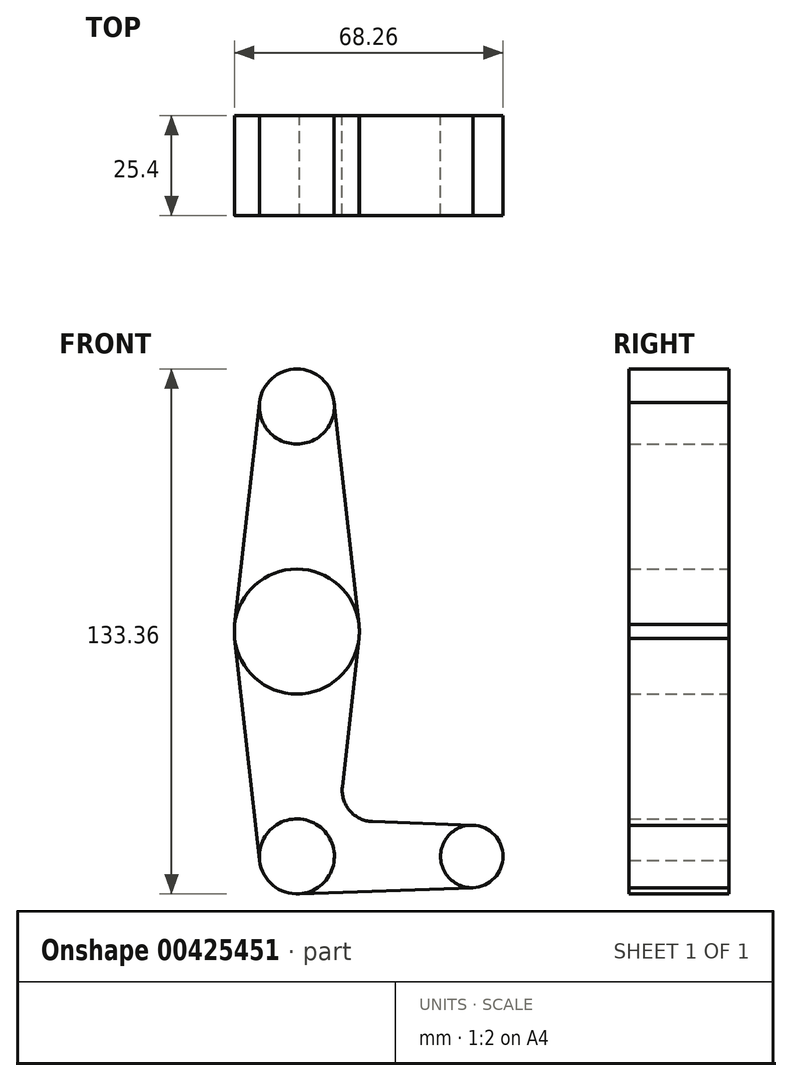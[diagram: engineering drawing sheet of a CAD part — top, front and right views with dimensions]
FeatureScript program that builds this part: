
annotation { "Feature Type Name" : "Feature", "Feature Type Description" : "" }
export const myFeature = defineFeature(function(context is Context, id is Id, definition is map)
    precondition{}
    {
        {
            var Q0;
            Q0=qCreatedBy(makeId("Front.planeOp"),FACE);
            var sketch = newSketch(context, id + "F0", { "sketchPlane" : qUnion([Q0])});
            skLineSegment(sketch, "E0", {"start": v(0, 114.3) * mm, "end": v(0, 0) * mm, "construction": true});
            skLineSegment(sketch, "E1", {"start": v(0, 0) * mm, "end": v(44.45, 0) * mm, "construction": true});
            skCircle(sketch, "E2", {"center": v(0, 114.3) * mm, "radius": 9.53 * mm});
            skCircle(sketch, "E3", {"center": v(0, 57.15) * mm, "radius": 15.88 * mm});
            skCircle(sketch, "E4", {"center": v(0, 0) * mm, "radius": 9.53 * mm});
            skCircle(sketch, "E5", {"center": v(44.45, 0) * mm, "radius": 7.94 * mm});
            skLineSegment(sketch, "E6", {"start": v(-9.47, 115.36) * mm, "end": v(-15.78, 58.91) * mm});
            skLineSegment(sketch, "E7", {"start": v(9.47, 115.36) * mm, "end": v(15.78, 58.91) * mm});
            skLineSegment(sketch, "E8", {"start": v(-15.78, 55.39) * mm, "end": v(-9.58, 0) * mm});
            skLineSegment(sketch, "E9", {"start": v(15.78, 55.39) * mm, "end": v(11.56, 17.67) * mm});
            skLineSegment(sketch, "E10", {"start": v(0, -9.52) * mm, "end": v(44.73, -7.93) * mm});
            skLineSegment(sketch, "E11", {"start": v(19.18, 8.85) * mm, "end": v(44.73, 7.93) * mm});
            skArc(sketch, "E12.filletArc", {"start": v(11.56, 17.67) * mm, "mid": v(13.44, 11.6) * mm, "end": v(19.18, 8.85) * mm});
            skLineSegment(sketch, "E13", {"start": v(-9.58, 0) * mm, "end": v(-9.47, -1.06) * mm});
            skSolve(sketch);
        }
        {
            var Q0;
            {var subQ0=sQuery(id+"F0.wireOp",EDGE,"E6");Q0=makeQuery(id+"F0.imprint","IMPRINT",FACE,{"disambiguationData":[TD([[makeQuery(id+"F0.imprint","IMPRINT",EDGE,{"derivedFrom":subQ0}),1.0]])]});}
            var Q1;
            {var subQ0=sQuery(id+"F0.wireOp",EDGE,"E8");Q1=makeQuery(id+"F0.imprint","IMPRINT",FACE,{"disambiguationData":[TD([[makeQuery(id+"F0.imprint","IMPRINT",EDGE,{"derivedFrom":subQ0}),1.0]])]});}
            extrude(context, id + "F1", {"entities" : qUnion([Q0, Q1]), "depth" : 25.4 * mm});
        }
        {
            var Q0;
            Q0 = qSketchRegion(id + "F0", true);
            extrude(context, id + "F2", {"entities" : qUnion([Q0]), "depth" : 25.4 * mm});
        }
    });
